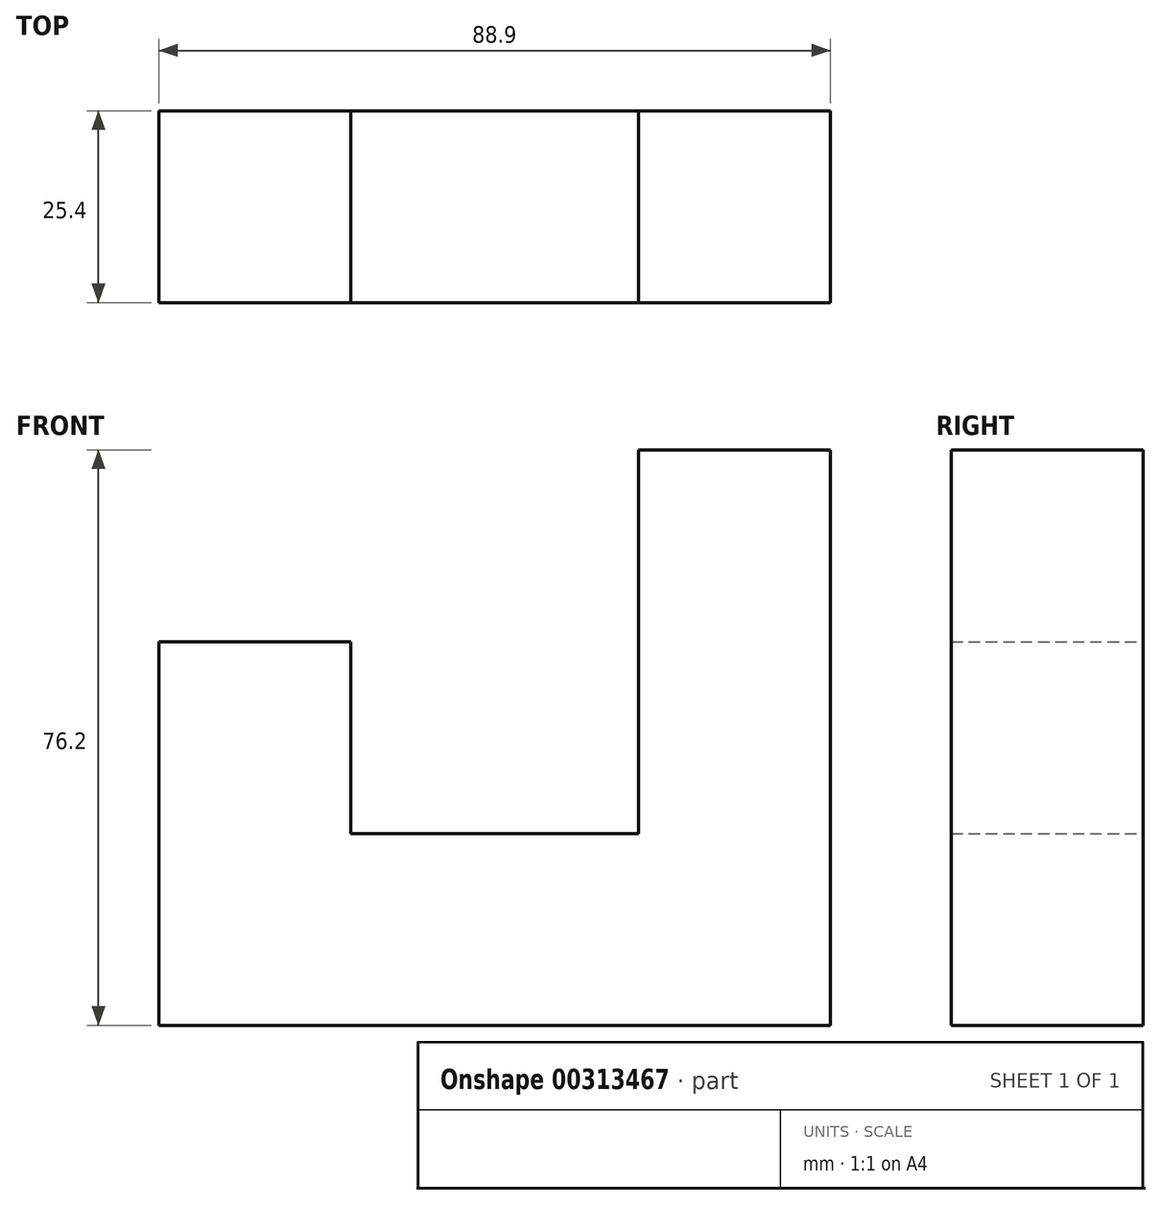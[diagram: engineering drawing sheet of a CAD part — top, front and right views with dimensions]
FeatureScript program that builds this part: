
annotation { "Feature Type Name" : "Feature", "Feature Type Description" : "" }
export const myFeature = defineFeature(function(context is Context, id is Id, definition is map)
    precondition{}
    {
        {
            var Q0;
            Q0=qCreatedBy(makeId("Front.planeOp"),FACE);
            var sketch = newSketch(context, id + "F0", { "sketchPlane" : qUnion([Q0])});
            skLineSegment(sketch, "E0", {"start": v(-41.2, -40.2) * mm, "end": v(47.7, -40.2) * mm});
            skLineSegment(sketch, "E1", {"start": v(47.7, -40.2) * mm, "end": v(47.7, 36) * mm});
            skLineSegment(sketch, "E2", {"start": v(47.7, 36) * mm, "end": v(22.3, 36) * mm});
            skLineSegment(sketch, "E3", {"start": v(22.3, 36) * mm, "end": v(22.3, -14.8) * mm});
            skLineSegment(sketch, "E4", {"start": v(22.3, -14.8) * mm, "end": v(-15.8, -14.8) * mm});
            skLineSegment(sketch, "E5", {"start": v(-15.8, -14.8) * mm, "end": v(-15.8, 10.6) * mm});
            skLineSegment(sketch, "E6", {"start": v(-15.8, 10.6) * mm, "end": v(-41.2, 10.6) * mm});
            skLineSegment(sketch, "E7", {"start": v(-41.2, 10.6) * mm, "end": v(-41.2, -40.2) * mm});
            skSolve(sketch);
        }
        {
            var Q0;
            Q0=makeQuery(id+"F0.imprint","IMPRINT",FACE,{"disambiguationData":[TD([[makeQuery(id+"F0.imprint","IMPRINT",EDGE,{"derivedFrom":sQuery(id+"F0.wireOp",EDGE,"E0")}),1.0]])]});
            extrude(context, id + "F1", {"entities" : qUnion([Q0]), "depth" : 25.4 * mm});
        }
    });
